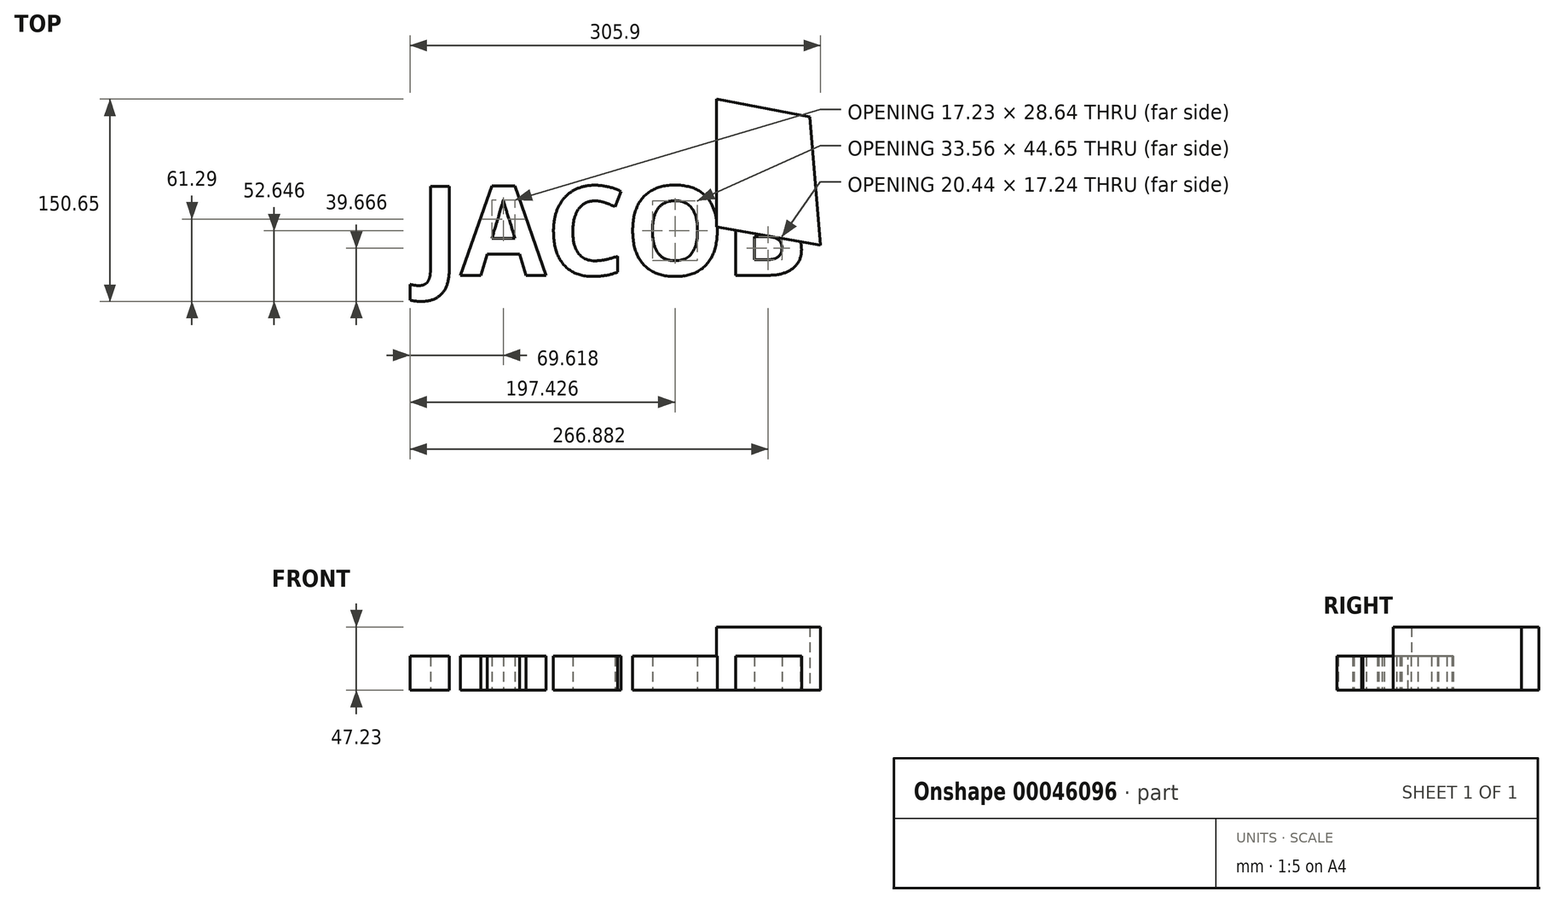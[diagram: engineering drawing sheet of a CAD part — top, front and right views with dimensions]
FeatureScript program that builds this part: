
annotation { "Feature Type Name" : "Feature", "Feature Type Description" : "" }
export const myFeature = defineFeature(function(context is Context, id is Id, definition is map)
    precondition{}
    {
        {
            var Q0;
            Q0=qCreatedBy(makeId("Top.planeOp"),FACE);
            var sketch = newSketch(context, id + "F0", { "sketchPlane" : qUnion([Q0])});
            skLineSegment(sketch, "E0", {"start": v(61.15, 77.26) * mm, "end": v(61.15, -17.93) * mm});
            skLineSegment(sketch, "E1", {"start": v(61.15, -17.93) * mm, "end": v(138.62, -31.52) * mm});
            skLineSegment(sketch, "E2", {"start": v(138.62, -31.52) * mm, "end": v(130.5, 64.09) * mm});
            skLineSegment(sketch, "E3", {"start": v(130.5, 64.09) * mm, "end": v(61.15, 77.26) * mm});
            skSolve(sketch);
        }
        {
            var Q0;
            Q0=makeQuery(id+"F0.imprint","IMPRINT",FACE,{"disambiguationData":[TD([[makeQuery(id+"F0.imprint","IMPRINT",EDGE,{"derivedFrom":sQuery(id+"F0.wireOp",EDGE,"E0")}),1.0]])]});
            extrude(context, id + "F1", {"entities" : qUnion([Q0]), "depth" : 47.23 * mm});
        }
        {
            var Q0;
            Q0=qCreatedBy(makeId("Top.planeOp"),FACE);
            var sketch = newSketch(context, id + "F2", { "sketchPlane" : qUnion([Q0])});
            skText(sketch, "E4", { "text": "JACOB", "fontName": "OpenSans-Bold.ttf"});
            const initialGuessF2  = {"E4": [-0.1604, -0.05393, 1, 0, 0.06672]};
            skSetInitialGuess(sketch, initialGuessF2);
            skSolve(sketch);
        }
        {
            var Q0;
            Q0 = qSketchRegion(id + "F2", true);
            extrude(context, id + "F3", {"entities" : qUnion([Q0]), "operationType" : NewBodyOperationType.ADD, "depth" : 25.4 * mm});
        }
    });
